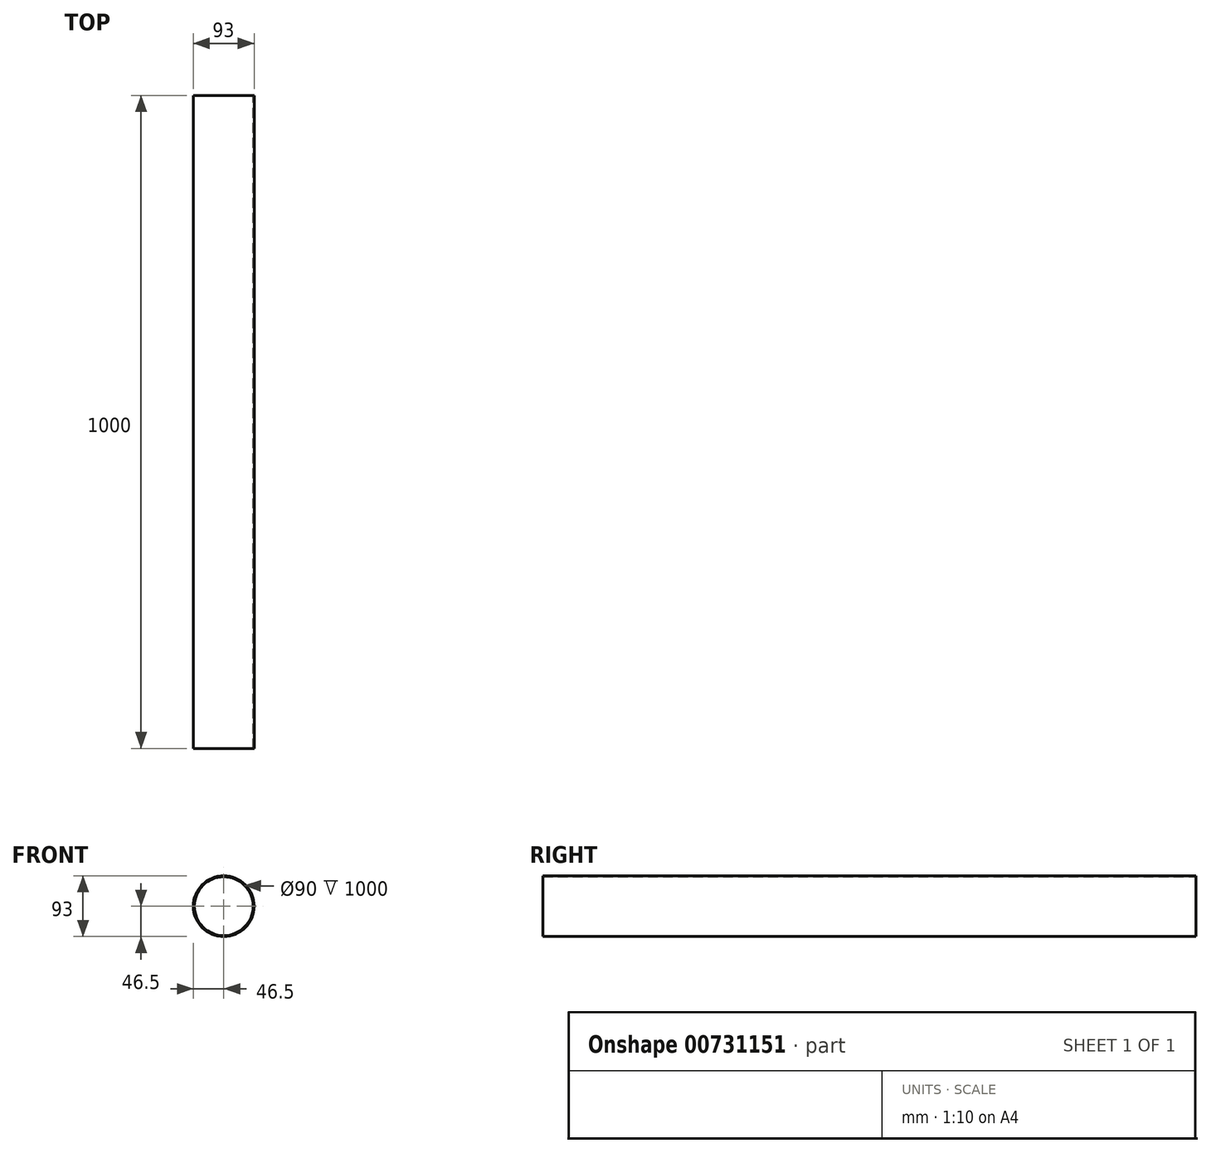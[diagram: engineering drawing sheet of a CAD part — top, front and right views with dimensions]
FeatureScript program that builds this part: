
annotation { "Feature Type Name" : "Feature", "Feature Type Description" : "" }
export const myFeature = defineFeature(function(context is Context, id is Id, definition is map)
    precondition{}
    {
        {
            var Q0;
            Q0=qCreatedBy(makeId("Front.planeOp"),FACE);
            var sketch = newSketch(context, id + "F0", { "sketchPlane" : qUnion([Q0])});
            skCircle(sketch, "E0", {"center": v(0, 0) * mm, "radius": 45 * mm});
            skCircle(sketch, "E1", {"center": v(0, 0) * mm, "radius": 46.5 * mm});
            skSolve(sketch);
        }
        {
            var Q0;
            Q0=qSketchRegion(id+"F0",true);
            extrude(context, id + "F1", {"entities" : qUnion([Q0]), "depth" : 1000 * mm, "offsetDistance" : 25 * mm});
        }
    });
